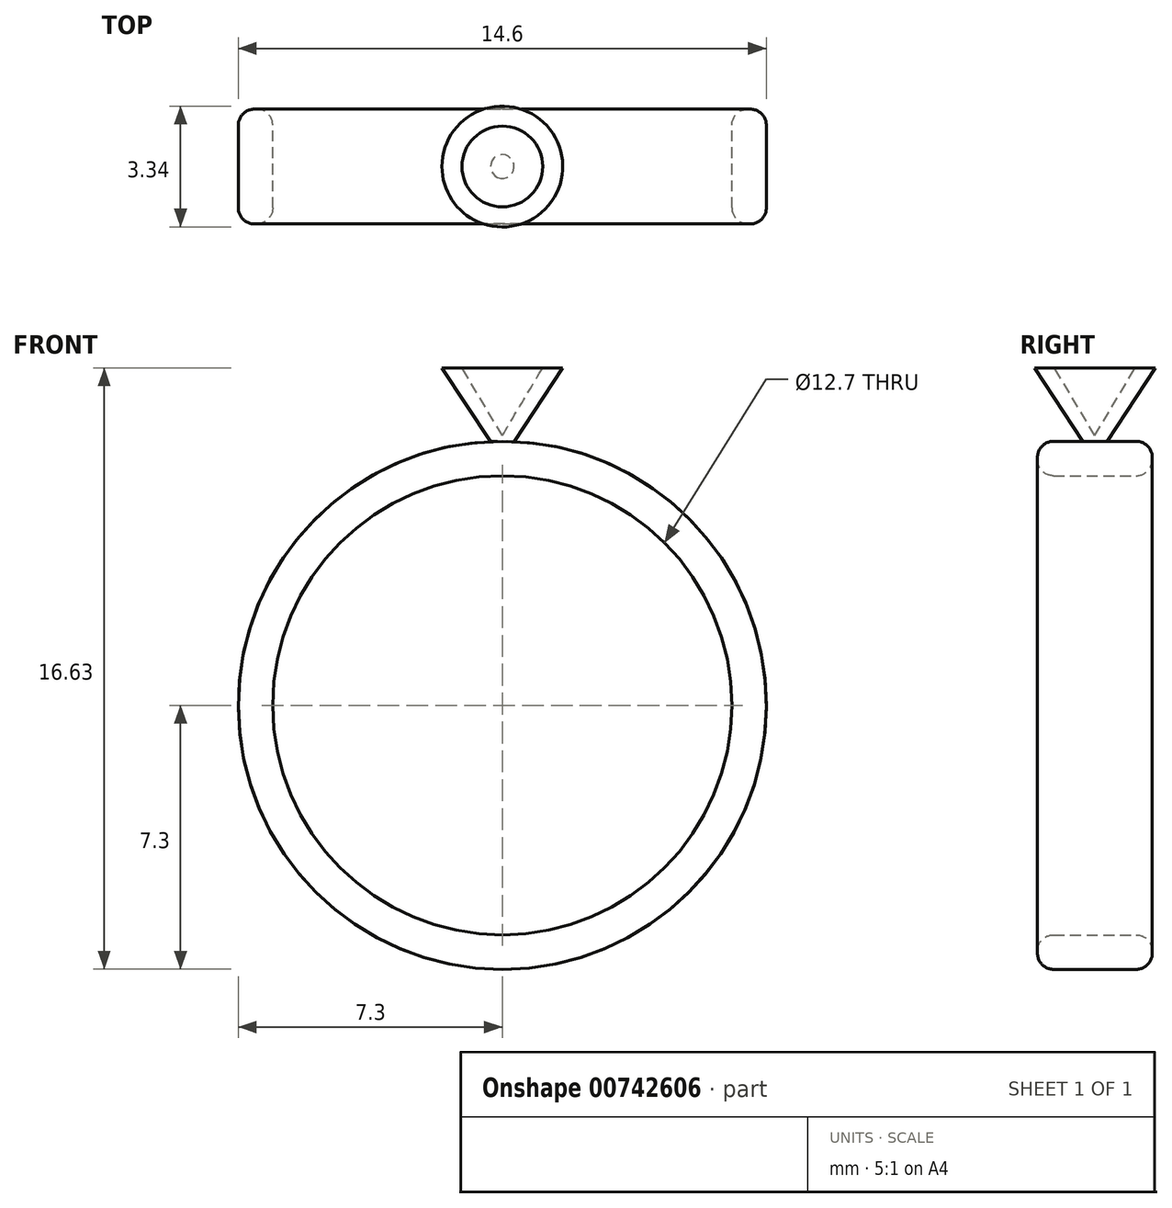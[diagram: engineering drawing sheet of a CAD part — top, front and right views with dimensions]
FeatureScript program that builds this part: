
annotation { "Feature Type Name" : "Feature", "Feature Type Description" : "" }
export const myFeature = defineFeature(function(context is Context, id is Id, definition is map)
    precondition{}
    {
        {
            var Q0;
            Q0=qCreatedBy(makeId("Front.planeOp"),FACE);
            var sketch = newSketch(context, id + "F0", { "sketchPlane" : qUnion([Q0])});
            skCircle(sketch, "E0", {"center": v(0, 0) * mm, "radius": 7.3 * mm});
            skCircle(sketch, "E1", {"center": v(0, 0) * mm, "radius": 6.35 * mm});
            skSolve(sketch);
        }
        {
            var Q0;
            Q0 = qSketchRegion(id + "F0", true);
            extrude(context, id + "F1", {"entities" : qUnion([Q0]), "endBound" : BoundingType.SYMMETRIC, "depth" : 3.17 * mm, "offsetDistance" : 25.4 * mm});
        }
        {
            var Q0;
            Q0=makeQuery(id+"F1.opExtrude","CAP_FACE",FACE,{"disambiguationData":[OSD([sQuery(id+"F0.wireOp",EDGE,"E0"),sQuery(id+"F0.wireOp",EDGE,"E1")])],"isStart":false});
            var Q1;
            Q1=makeQuery(id+"F1.opExtrude","CAP_FACE",FACE,{"disambiguationData":[OSD([sQuery(id+"F0.wireOp",EDGE,"E0"),sQuery(id+"F0.wireOp",EDGE,"E1")])],"isStart":true});
            fillet(context, id + "F2", {"entities" : qUnion([Q0, Q1]), "radius" : 0.44 * mm, "tangentPropagation" : true, "allowEdgeOverflow" : false});
        }
        {
            var Q0;
            Q0=qCreatedBy(makeId("Front.planeOp"),FACE);
            var sketch = newSketch(context, id + "F3", { "sketchPlane" : qUnion([Q0])});
            skLineSegment(sketch, "E2", {"start": v(0, 6.8) * mm, "end": v(0, 9.33) * mm});
            skLineSegment(sketch, "E3", {"start": v(0, 9.33) * mm, "end": v(1.67, 9.33) * mm});
            skLineSegment(sketch, "E4", {"start": v(1.67, 9.33) * mm, "end": v(0, 6.8) * mm});
            skSolve(sketch);
        }
        {
            var Q0;
            Q0=makeQuery(id+"F3.imprint","IMPRINT",FACE,{"disambiguationData":[TD([[makeQuery(id+"F3.imprint","IMPRINT",EDGE,{"derivedFrom":sQuery(id+"F3.wireOp",EDGE,"E2")}),-1.0]])]});
            var Q1;
            Q1=sQuery(id+"F3.wireOp",EDGE,"E2");
            revolve(context, id + "F4", {"operationType" : NewBodyOperationType.ADD, "surfaceOperationType" : NewSurfaceOperationType.NEW, "entities" : qUnion([Q0]), "axis" : qUnion([Q1]), "revolveType" : RevolveType.FULL});
        }
        {
            var Q0;
            Q0=qCreatedBy(makeId("Front.planeOp"),FACE);
            var sketch = newSketch(context, id + "F5", { "sketchPlane" : qUnion([Q0])});
            skLineSegment(sketch, "E5", {"start": v(0, 9.83) * mm, "end": v(1.41, 9.83) * mm});
            skLineSegment(sketch, "E6", {"start": v(1.41, 9.83) * mm, "end": v(0, 7.46) * mm});
            skLineSegment(sketch, "E7", {"start": v(0, 7.46) * mm, "end": v(0, 9.83) * mm});
            skSolve(sketch);
        }
        {
            var Q0;
            Q0=makeQuery(id+"F5.imprint","IMPRINT",FACE,{"disambiguationData":[TD([[makeQuery(id+"F5.imprint","IMPRINT",EDGE,{"derivedFrom":sQuery(id+"F5.wireOp",EDGE,"E5")}),-1.0]])]});
            var Q1;
            Q1=sQuery(id+"F5.wireOp",EDGE,"E7");
            revolve(context, id + "F6", {"operationType" : NewBodyOperationType.REMOVE, "surfaceOperationType" : NewSurfaceOperationType.NEW, "entities" : qUnion([Q0]), "axis" : qUnion([Q1]), "revolveType" : RevolveType.FULL, "oppositeDirection" : true});
        }
    });
